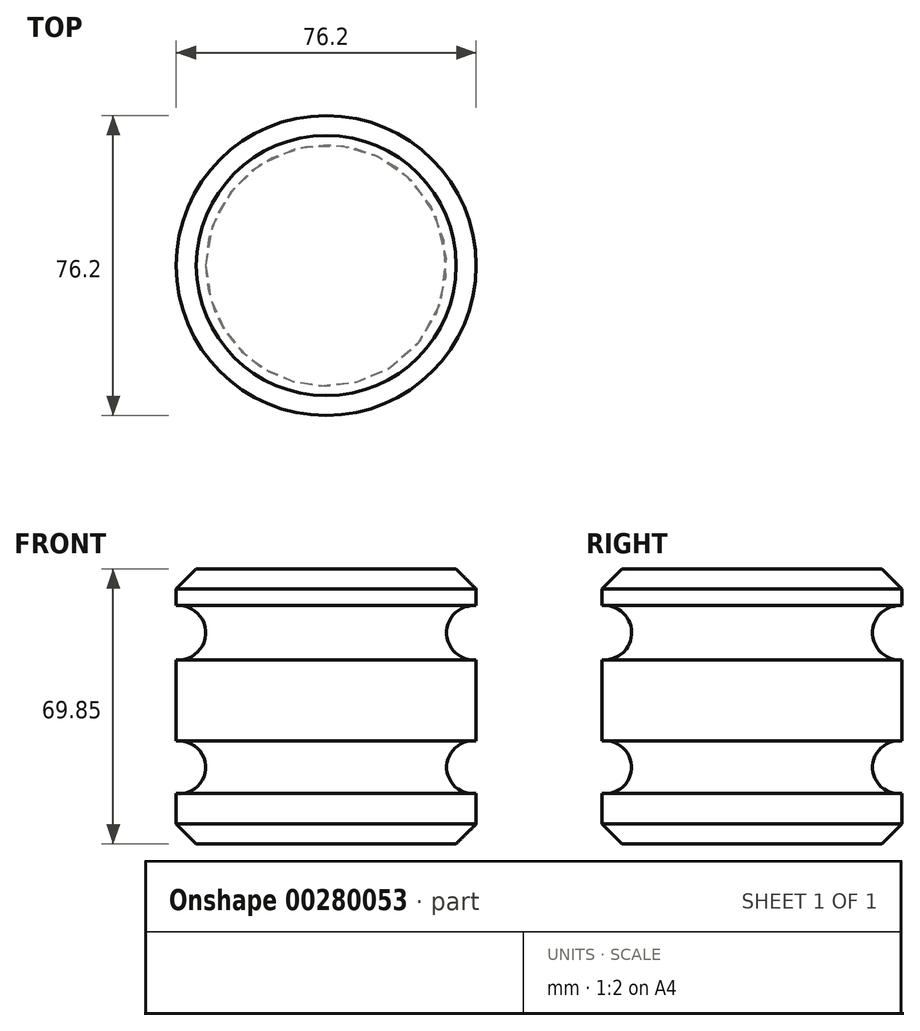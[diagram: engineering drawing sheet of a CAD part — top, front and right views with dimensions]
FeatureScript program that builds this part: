
annotation { "Feature Type Name" : "Feature", "Feature Type Description" : "" }
export const myFeature = defineFeature(function(context is Context, id is Id, definition is map)
    precondition{}
    {
        {
            var Q0;
            Q0=qCreatedBy(makeId("Front.planeOp"),FACE);
            var sketch = newSketch(context, id + "F0", { "sketchPlane" : qUnion([Q0])});
            skLineSegment(sketch, "E0.bottom", {"start": v(0, 0) * mm, "end": v(-38.1, 0) * mm});
            skLineSegment(sketch, "E0.top", {"start": v(0, 69.85) * mm, "end": v(-38.1, 69.85) * mm});
            skLineSegment(sketch, "E0.left", {"start": v(0, 0) * mm, "end": v(0, 12.8) * mm});
            skLineSegment(sketch, "E0.right", {"start": v(-38.1, 0) * mm, "end": v(-38.1, 69.85) * mm});
            skArc(sketch, "E1", {"start": v(0, 60.53) * mm, "mid": v(-7.51, 53.66) * mm, "end": v(0, 46.78) * mm});
            skArc(sketch, "E2", {"start": v(0, 26.16) * mm, "mid": v(-7.48, 19.48) * mm, "end": v(0, 12.8) * mm});
            skLineSegment(sketch, "E3.trimOffspring", {"start": v(0, 60.53) * mm, "end": v(0, 69.85) * mm});
            skLineSegment(sketch, "E4.trimOffspring", {"start": v(0, 26.16) * mm, "end": v(0, 46.78) * mm});
            skSolve(sketch);
        }
        {
            var Q0;
            Q0 = qSketchRegion(id + "F0", true);
            var Q1;
            Q1=sQuery(id+"F0.wireOp",EDGE,"E0.right");
            revolve(context, id + "F1", {"entities" : qUnion([Q0]), "axis" : qUnion([Q1]), "revolveType" : RevolveType.FULL});
        }
        {
            var Q0;
            Q0=makeQuery(id+"F1.opRevolve","SWEPT_EDGE",EDGE,{"disambiguationData":[OSD([sQuery(id+"F0.wireOp",EDGE,"E0.top"),sQuery(id+"F0.wireOp",EDGE,"E3.trimOffspring")])]});
            var Q1;
            Q1=makeQuery(id+"F1.opRevolve","SWEPT_EDGE",EDGE,{"disambiguationData":[OSD([sQuery(id+"F0.wireOp",EDGE,"E0.bottom"),sQuery(id+"F0.wireOp",EDGE,"E0.left")])]});
            chamfer(context, id + "F2", {"entities" : qUnion([Q0, Q1]), "width" : 5.08 * mm, "tangentPropagation" : true});
        }
    });
